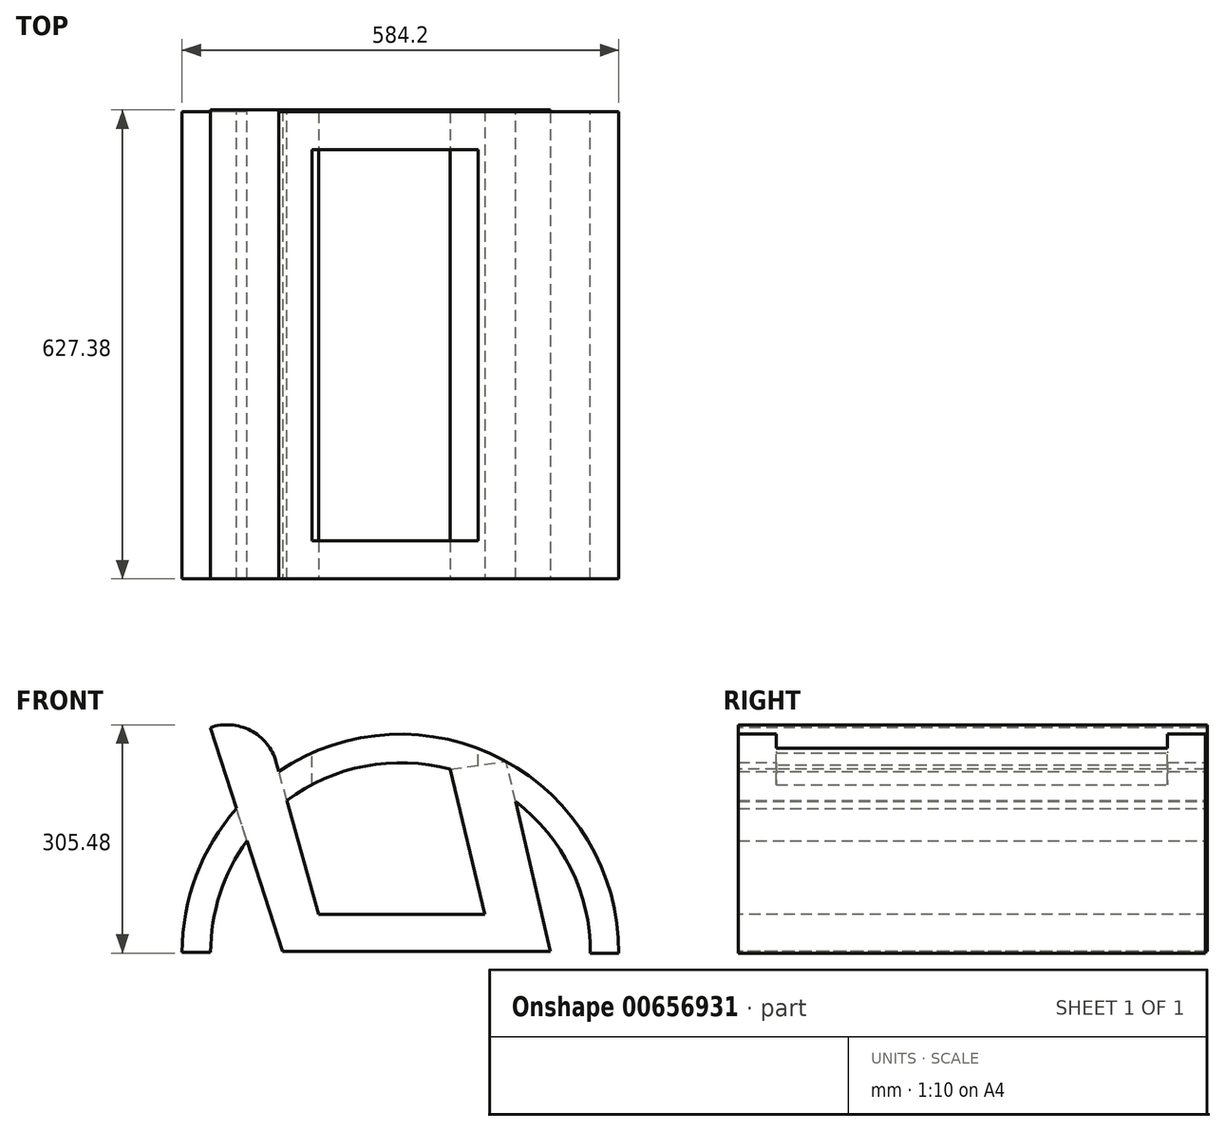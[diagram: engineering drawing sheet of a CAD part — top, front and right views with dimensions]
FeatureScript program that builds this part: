
annotation { "Feature Type Name" : "Feature", "Feature Type Description" : "" }
export const myFeature = defineFeature(function(context is Context, id is Id, definition is map)
    precondition{}
    {
        {
            var Q0;
            Q0=qCreatedBy(makeId("Front.planeOp"),FACE);
            var sketch = newSketch(context, id + "F0", { "sketchPlane" : qUnion([Q0])});
            skArc(sketch, "E0", {"start": v(401.64, -301.65) * mm, "mid": v(109.9, -8.81) * mm, "end": v(-182.56, -300.91) * mm});
            skArc(sketch, "E1", {"start": v(363.54, -301.65) * mm, "mid": v(109.9, -46.91) * mm, "end": v(-144.46, -300.91) * mm});
            skLineSegment(sketch, "E2", {"start": v(401.64, -301.65) * mm, "end": v(363.54, -301.65) * mm});
            skLineSegment(sketch, "E3", {"start": v(-182.56, -300.91) * mm, "end": v(-144.46, -300.91) * mm});
            skPoint(sketch, "E4.startSnap0", {"position": v(109.9, -8.81) * mm});
            skSolve(sketch);
        }
        {
            var Q0;
            Q0=qSketchRegion(id+"F0",true);
            extrude(context, id + "F1", {"entities" : qUnion([Q0]), "depth" : 624.84 * mm, "offsetDistance" : 25.4 * mm});
        }
        {
            var Q0;
            Q0=makeQuery(id+"F1.opExtrude","CAP_FACE",FACE,{"disambiguationData":[OSD([sQuery(id+"F0.wireOp",EDGE,"E0"),sQuery(id+"F0.wireOp",EDGE,"E1"),sQuery(id+"F0.wireOp",EDGE,"E2"),sQuery(id+"F0.wireOp",EDGE,"E3")])],"isStart":false});
            var sketch = newSketch(context, id + "F2", { "sketchPlane" : qUnion([Q0])});
            skLineSegment(sketch, "E5", {"start": v(222.5, -249.83) * mm, "end": v(0, -249.83) * mm});
            skLineSegment(sketch, "E6", {"start": v(310.08, -299.21) * mm, "end": v(-48.14, -299.21) * mm});
            skLineSegment(sketch, "E7", {"start": v(-48.14, -299.21) * mm, "end": v(-145.07, 0) * mm});
            skLineSegment(sketch, "E8", {"start": v(222.5, -249.83) * mm, "end": v(176.1, -55.79) * mm});
            skLineSegment(sketch, "E9", {"start": v(310.08, -299.21) * mm, "end": v(251, -45.35) * mm});
            skLineSegment(sketch, "E10", {"start": v(176.1, -55.79) * mm, "end": v(251, -45.35) * mm});
            skLineSegment(sketch, "E11", {"start": v(0, -249.83) * mm, "end": v(-56.98, -45.95) * mm});
            skArc(sketch, "E12", {"start": v(-56.98, -45.95) * mm, "mid": v(-91.07, -3.9) * mm, "end": v(-145.07, 0) * mm});
            skSolve(sketch);
        }
        {
            var Q0;
            Q0=qCreatedBy(makeId("Top.planeOp"),FACE);
            var sketch = newSketch(context, id + "F3", { "sketchPlane" : qUnion([Q0])});
            skLineSegment(sketch, "E13.bottom", {"start": v(-8.87, -50.8) * mm, "end": v(213.37, -50.8) * mm});
            skLineSegment(sketch, "E13.top", {"start": v(-8.87, -574.04) * mm, "end": v(213.37, -574.04) * mm});
            skLineSegment(sketch, "E13.left", {"start": v(-8.87, -50.8) * mm, "end": v(-8.87, -574.04) * mm});
            skLineSegment(sketch, "E13.right", {"start": v(213.37, -50.8) * mm, "end": v(213.37, -574.04) * mm});
            skSolve(sketch);
        }
        {
            var Q0;
            Q0=makeQuery(id+"F3.imprint","IMPRINT",FACE,{"disambiguationData":[TD([[makeQuery(id+"F3.imprint","IMPRINT",EDGE,{"derivedFrom":sQuery(id+"F3.wireOp",EDGE,"E13.bottom")}),-1.0]])]});
            extrude(context, id + "F4", {"entities" : qUnion([Q0]), "operationType" : NewBodyOperationType.REMOVE, "oppositeDirection" : true, "depth" : 99.06 * mm, "offsetDistance" : 25.4 * mm});
        }
        {
            var Q0;
            Q0 = qSketchRegion(id + "F2", true);
            extrude(context, id + "F5", {"entities" : qUnion([Q0]), "operationType" : NewBodyOperationType.ADD, "oppositeDirection" : true, "depth" : 627.38 * mm, "offsetDistance" : 25.4 * mm});
        }
    });
